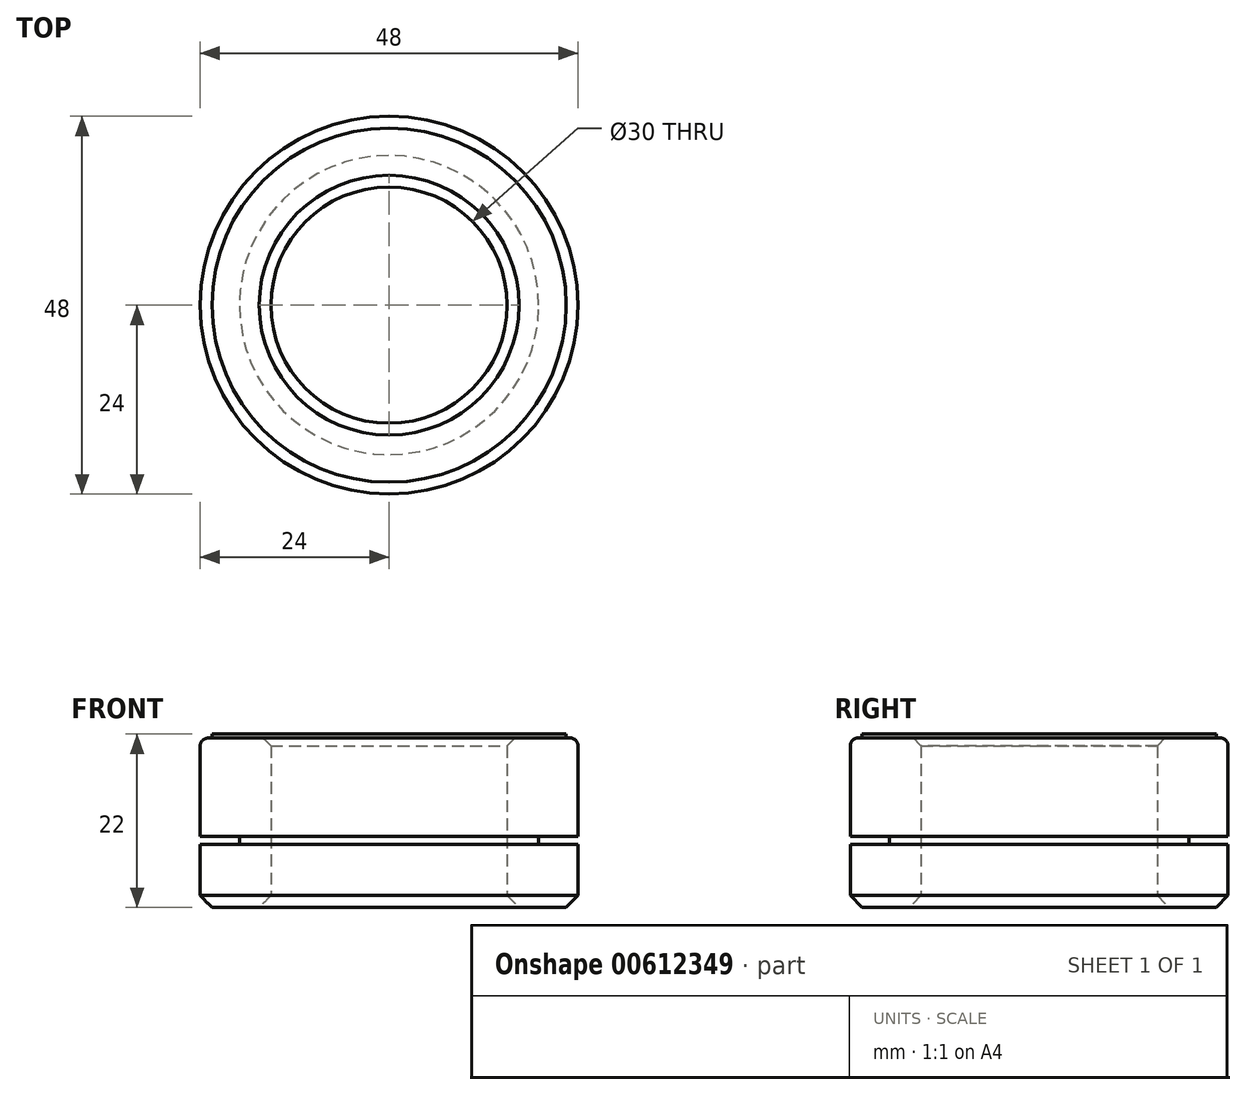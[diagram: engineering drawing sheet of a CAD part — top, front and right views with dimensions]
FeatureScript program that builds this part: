
annotation { "Feature Type Name" : "Feature", "Feature Type Description" : "" }
export const myFeature = defineFeature(function(context is Context, id is Id, definition is map)
    precondition{}
    {
        {
            var Q0;
            Q0=qCreatedBy(makeId("Front.planeOp"),FACE);
            var sketch = newSketch(context, id + "F0", { "sketchPlane" : qUnion([Q0])});
            skLineSegment(sketch, "E0", {"start": v(0, -7.05) * mm, "end": v(0, 0) * mm});
            skLineSegment(sketch, "E1", {"start": v(15, 0) * mm, "end": v(15, 22) * mm});
            skLineSegment(sketch, "E2", {"start": v(15, 22) * mm, "end": v(22.5, 22) * mm});
            skLineSegment(sketch, "E3", {"start": v(22.5, 22) * mm, "end": v(22.5, 21.5) * mm});
            skLineSegment(sketch, "E4", {"start": v(22.5, 21.5) * mm, "end": v(24, 21.5) * mm});
            skLineSegment(sketch, "E5", {"start": v(24, 21.5) * mm, "end": v(24, 9) * mm});
            skLineSegment(sketch, "E6", {"start": v(24, 9) * mm, "end": v(19, 9) * mm});
            skLineSegment(sketch, "E7", {"start": v(19, 9) * mm, "end": v(19, 8) * mm});
            skLineSegment(sketch, "E8", {"start": v(19, 8) * mm, "end": v(24, 8) * mm});
            skLineSegment(sketch, "E9", {"start": v(24, 8) * mm, "end": v(24, 0) * mm});
            skLineSegment(sketch, "E10", {"start": v(15, 0) * mm, "end": v(24, 0) * mm});
            skSolve(sketch);
        }
        {
            var Q0;
            Q0=makeQuery(id+"F0.imprint","IMPRINT",FACE,{"disambiguationData":[TD([[makeQuery(id+"F0.imprint","IMPRINT",EDGE,{"derivedFrom":sQuery(id+"F0.wireOp",EDGE,"E1")}),-1.0]])]});
            var Q1;
            Q1=sQuery(id+"F0.wireOp",EDGE,"E0");
            revolve(context, id + "F1", {"entities" : qUnion([Q0]), "axis" : qUnion([Q1]), "revolveType" : RevolveType.FULL});
        }
        {
            var Q0;
            Q0=makeQuery(id+"F1.opRevolve","SWEPT_EDGE",EDGE,{"disambiguationData":[OSD([sQuery(id+"F0.wireOp",EDGE,"E9"),sQuery(id+"F0.wireOp",EDGE,"E10")])]});
            var Q1;
            Q1=makeQuery(id+"F1.opRevolve","SWEPT_EDGE",EDGE,{"disambiguationData":[OSD([sQuery(id+"F0.wireOp",EDGE,"E1"),sQuery(id+"F0.wireOp",EDGE,"E10")])]});
            var Q2;
            Q2=makeQuery(id+"F1.opRevolve","SWEPT_EDGE",EDGE,{"disambiguationData":[OSD([sQuery(id+"F0.wireOp",EDGE,"E1"),sQuery(id+"F0.wireOp",EDGE,"E2")])]});
            chamfer(context, id + "F2", {"entities" : qUnion([Q0, Q1, Q2]), "width" : 1.5 * mm, "tangentPropagation" : true});
        }
        {
            var Q0;
            Q0=makeQuery(id+"F1.opRevolve","SWEPT_EDGE",EDGE,{"disambiguationData":[OSD([sQuery(id+"F0.wireOp",EDGE,"E4"),sQuery(id+"F0.wireOp",EDGE,"E5")])]});
            fillet(context, id + "F3", {"entities" : qUnion([Q0]), "radius" : 1 * mm, "tangentPropagation" : true, "allowEdgeOverflow" : false});
        }
    });
